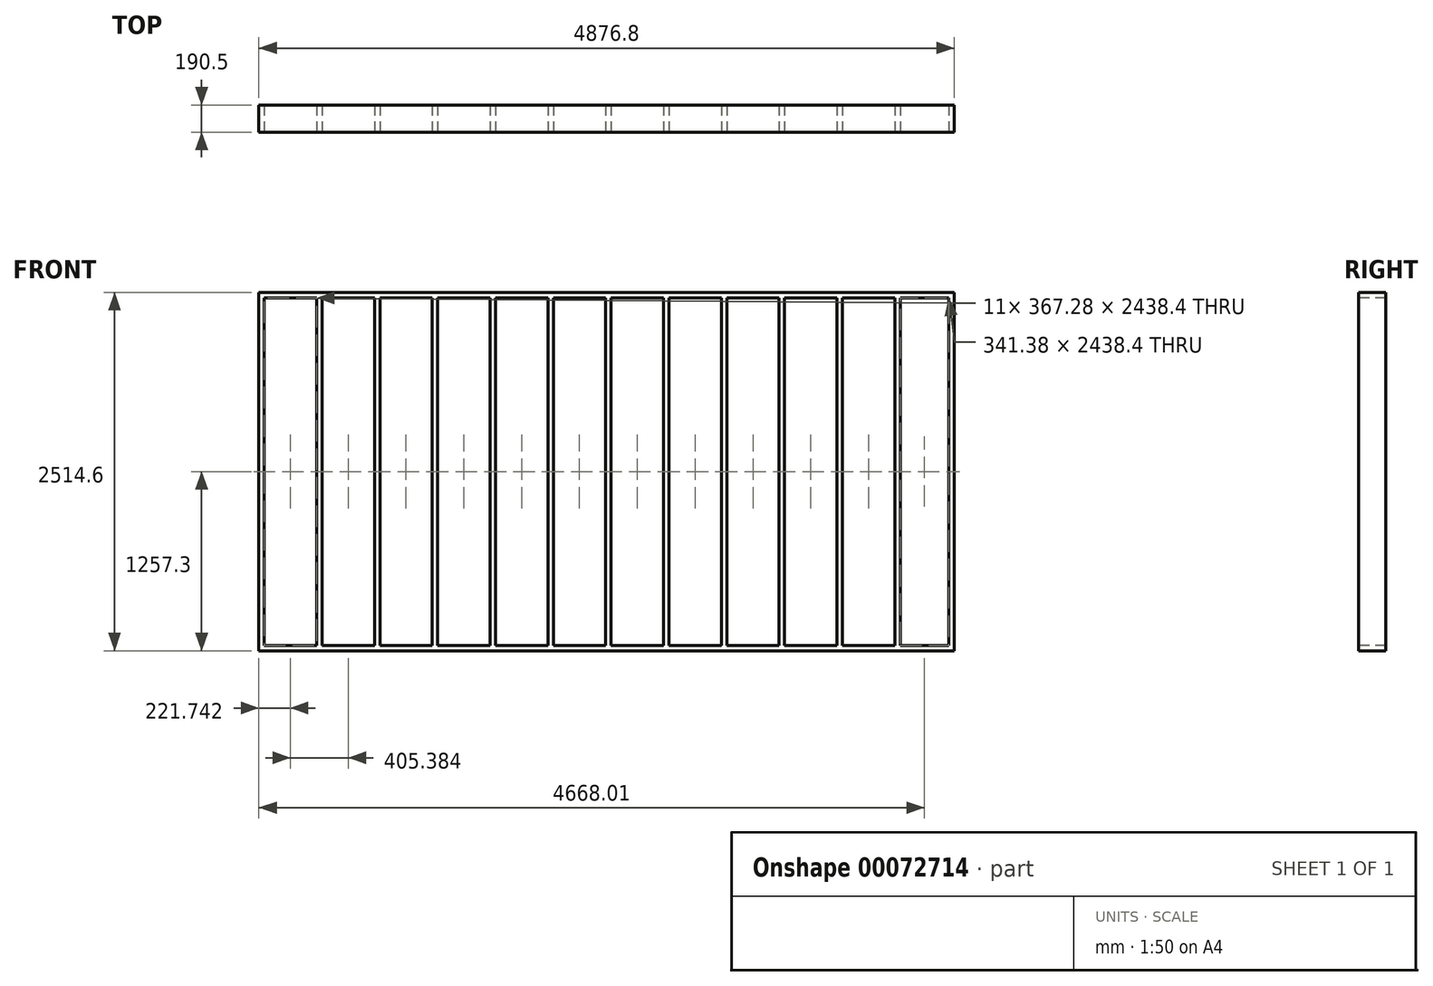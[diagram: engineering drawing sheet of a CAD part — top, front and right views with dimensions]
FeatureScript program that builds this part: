
annotation { "Feature Type Name" : "Feature", "Feature Type Description" : "" }
export const myFeature = defineFeature(function(context is Context, id is Id, definition is map)
    precondition{}
    {
        {
            var Q0;
            Q0=qCreatedBy(makeId("Top.planeOp"),FACE);
            var sketch = newSketch(context, id + "F0", { "sketchPlane" : qUnion([Q0])});
            skLineSegment(sketch, "E0.bottom", {"start": v(0, 0) * mm, "end": v(4876.8, 0) * mm});
            skLineSegment(sketch, "E0.top", {"start": v(0, 190.5) * mm, "end": v(4876.8, 190.5) * mm});
            skLineSegment(sketch, "E0.left", {"start": v(0, 0) * mm, "end": v(0, 190.5) * mm});
            skLineSegment(sketch, "E0.right", {"start": v(4876.8, 0) * mm, "end": v(4876.8, 190.5) * mm});
            skSolve(sketch);
        }
        {
            var Q0;
            Q0=makeQuery(id+"F0.imprint","IMPRINT",FACE,{"disambiguationData":[TD([[makeQuery(id+"F0.imprint","IMPRINT",EDGE,{"derivedFrom":sQuery(id+"F0.wireOp",EDGE,"E0.bottom")}),1.0]])]});
            extrude(context, id + "F1", {"entities" : qUnion([Q0]), "depth" : 38.1 * mm});
        }
        {
            var Q0;
            Q0=makeQuery(id+"F1.opExtrude","CAP_FACE",FACE,{"disambiguationData":[OSD([sQuery(id+"F0.wireOp",EDGE,"E0.bottom"),sQuery(id+"F0.wireOp",EDGE,"E0.top"),sQuery(id+"F0.wireOp",EDGE,"E0.left"),sQuery(id+"F0.wireOp",EDGE,"E0.right")])],"isStart":false});
            var sketch = newSketch(context, id + "F2", { "sketchPlane" : qUnion([Q0])});
            skLineSegment(sketch, "E1.bottom", {"start": v(0, 190.5) * mm, "end": v(38.1, 190.5) * mm});
            skLineSegment(sketch, "E1.top", {"start": v(0, 0) * mm, "end": v(38.1, 0) * mm});
            skLineSegment(sketch, "E1.left", {"start": v(0, 190.5) * mm, "end": v(0, 0) * mm});
            skLineSegment(sketch, "E1.right", {"start": v(38.1, 190.5) * mm, "end": v(38.1, 0) * mm});
            skLineSegment(sketch, "E2.1.0.0", {"start": v(405.38, 190.5) * mm, "end": v(443.48, 190.5) * mm});
            skLineSegment(sketch, "E2.1.0.1", {"start": v(405.38, 0) * mm, "end": v(443.48, 0) * mm});
            skLineSegment(sketch, "E2.1.0.2", {"start": v(405.38, 190.5) * mm, "end": v(405.38, 0) * mm});
            skLineSegment(sketch, "E2.1.0.3", {"start": v(443.48, 190.5) * mm, "end": v(443.48, 0) * mm});
            skLineSegment(sketch, "E2.2.0.0", {"start": v(810.77, 190.5) * mm, "end": v(848.87, 190.5) * mm});
            skLineSegment(sketch, "E2.2.0.1", {"start": v(810.77, 0) * mm, "end": v(848.87, 0) * mm});
            skLineSegment(sketch, "E2.2.0.2", {"start": v(810.77, 190.5) * mm, "end": v(810.77, 0) * mm});
            skLineSegment(sketch, "E2.2.0.3", {"start": v(848.87, 190.5) * mm, "end": v(848.87, 0) * mm});
            skLineSegment(sketch, "E2.3.0.0", {"start": v(1216.15, 190.5) * mm, "end": v(1254.25, 190.5) * mm});
            skLineSegment(sketch, "E2.3.0.1", {"start": v(1216.15, 0) * mm, "end": v(1254.25, 0) * mm});
            skLineSegment(sketch, "E2.3.0.2", {"start": v(1216.15, 190.5) * mm, "end": v(1216.15, 0) * mm});
            skLineSegment(sketch, "E2.3.0.3", {"start": v(1254.25, 190.5) * mm, "end": v(1254.25, 0) * mm});
            skLineSegment(sketch, "E2.4.0.0", {"start": v(1621.54, 190.5) * mm, "end": v(1659.64, 190.5) * mm});
            skLineSegment(sketch, "E2.4.0.1", {"start": v(1621.54, 0) * mm, "end": v(1659.64, 0) * mm});
            skLineSegment(sketch, "E2.4.0.2", {"start": v(1621.54, 190.5) * mm, "end": v(1621.54, 0) * mm});
            skLineSegment(sketch, "E2.4.0.3", {"start": v(1659.64, 190.5) * mm, "end": v(1659.64, 0) * mm});
            skLineSegment(sketch, "E2.5.0.0", {"start": v(2026.92, 190.5) * mm, "end": v(2065.02, 190.5) * mm});
            skLineSegment(sketch, "E2.5.0.1", {"start": v(2026.92, 0) * mm, "end": v(2065.02, 0) * mm});
            skLineSegment(sketch, "E2.5.0.2", {"start": v(2026.92, 190.5) * mm, "end": v(2026.92, 0) * mm});
            skLineSegment(sketch, "E2.5.0.3", {"start": v(2065.02, 190.5) * mm, "end": v(2065.02, 0) * mm});
            skLineSegment(sketch, "E2.6.0.0", {"start": v(2432.3, 190.5) * mm, "end": v(2470.4, 190.5) * mm});
            skLineSegment(sketch, "E2.6.0.1", {"start": v(2432.3, 0) * mm, "end": v(2470.4, 0) * mm});
            skLineSegment(sketch, "E2.6.0.2", {"start": v(2432.3, 190.5) * mm, "end": v(2432.3, 0) * mm});
            skLineSegment(sketch, "E2.6.0.3", {"start": v(2470.4, 190.5) * mm, "end": v(2470.4, 0) * mm});
            skLineSegment(sketch, "E2.7.0.0", {"start": v(2837.69, 190.5) * mm, "end": v(2875.79, 190.5) * mm});
            skLineSegment(sketch, "E2.7.0.1", {"start": v(2837.69, 0) * mm, "end": v(2875.79, 0) * mm});
            skLineSegment(sketch, "E2.7.0.2", {"start": v(2837.69, 190.5) * mm, "end": v(2837.69, 0) * mm});
            skLineSegment(sketch, "E2.7.0.3", {"start": v(2875.79, 190.5) * mm, "end": v(2875.79, 0) * mm});
            skLineSegment(sketch, "E2.8.0.0", {"start": v(3243.07, 190.5) * mm, "end": v(3281.17, 190.5) * mm});
            skLineSegment(sketch, "E2.8.0.1", {"start": v(3243.07, 0) * mm, "end": v(3281.17, 0) * mm});
            skLineSegment(sketch, "E2.8.0.2", {"start": v(3243.07, 190.5) * mm, "end": v(3243.07, 0) * mm});
            skLineSegment(sketch, "E2.8.0.3", {"start": v(3281.17, 190.5) * mm, "end": v(3281.17, 0) * mm});
            skLineSegment(sketch, "E2.9.0.0", {"start": v(3648.46, 190.5) * mm, "end": v(3686.56, 190.5) * mm});
            skLineSegment(sketch, "E2.9.0.1", {"start": v(3648.46, 0) * mm, "end": v(3686.56, 0) * mm});
            skLineSegment(sketch, "E2.9.0.2", {"start": v(3648.46, 190.5) * mm, "end": v(3648.46, 0) * mm});
            skLineSegment(sketch, "E2.9.0.3", {"start": v(3686.56, 190.5) * mm, "end": v(3686.56, 0) * mm});
            skLineSegment(sketch, "E2.10.0.0", {"start": v(4053.84, 190.5) * mm, "end": v(4091.94, 190.5) * mm});
            skLineSegment(sketch, "E2.10.0.1", {"start": v(4053.84, 0) * mm, "end": v(4091.94, 0) * mm});
            skLineSegment(sketch, "E2.10.0.2", {"start": v(4053.84, 190.5) * mm, "end": v(4053.84, 0) * mm});
            skLineSegment(sketch, "E2.10.0.3", {"start": v(4091.94, 190.5) * mm, "end": v(4091.94, 0) * mm});
            skLineSegment(sketch, "E2.11.0.0", {"start": v(4459.22, 190.5) * mm, "end": v(4497.32, 190.5) * mm});
            skLineSegment(sketch, "E2.11.0.1", {"start": v(4459.22, 0) * mm, "end": v(4497.32, 0) * mm});
            skLineSegment(sketch, "E2.11.0.2", {"start": v(4459.22, 190.5) * mm, "end": v(4459.22, 0) * mm});
            skLineSegment(sketch, "E2.11.0.3", {"start": v(4497.32, 190.5) * mm, "end": v(4497.32, 0) * mm});
            skLineSegment(sketch, "E2.direction1", {"start": v(0, 190.5) * mm, "end": v(405.38, 190.5) * mm, "construction": true});
            skLineSegment(sketch, "E3.bottom", {"start": v(4876.8, 190.5) * mm, "end": v(4838.7, 190.5) * mm});
            skLineSegment(sketch, "E3.top", {"start": v(4876.8, 0) * mm, "end": v(4838.7, 0) * mm});
            skLineSegment(sketch, "E3.left", {"start": v(4876.8, 190.5) * mm, "end": v(4876.8, 0) * mm});
            skLineSegment(sketch, "E3.right", {"start": v(4838.7, 190.5) * mm, "end": v(4838.7, 0) * mm});
            skSolve(sketch);
        }
        {
            var Q0;
            Q0 = qSketchRegion(id + "F2", true);
            extrude(context, id + "F3", {"entities" : qUnion([Q0]), "operationType" : NewBodyOperationType.ADD, "depth" : 2438.4 * mm});
        }
        {
            var Q0;
            Q0=makeQuery(id+"F3.opExtrude","CAP_FACE",FACE,{"disambiguationData":[OSD([sQuery(id+"F2.wireOp",EDGE,"E1.bottom"),sQuery(id+"F2.wireOp",EDGE,"E1.top"),sQuery(id+"F2.wireOp",EDGE,"E1.left"),sQuery(id+"F2.wireOp",EDGE,"E1.right")])],"isStart":false});
            var sketch = newSketch(context, id + "F4", { "sketchPlane" : qUnion([Q0])});
            skLineSegment(sketch, "E4.bottom", {"start": v(0, 190.5) * mm, "end": v(4876.8, 190.5) * mm});
            skLineSegment(sketch, "E4.top", {"start": v(0, 0) * mm, "end": v(4876.8, 0) * mm});
            skLineSegment(sketch, "E4.left", {"start": v(0, 190.5) * mm, "end": v(0, 0) * mm});
            skLineSegment(sketch, "E4.right", {"start": v(4876.8, 190.5) * mm, "end": v(4876.8, 0) * mm});
            skSolve(sketch);
        }
        {
            var Q0;
            Q0 = qSketchRegion(id + "F4", true);
            extrude(context, id + "F5", {"entities" : qUnion([Q0]), "operationType" : NewBodyOperationType.ADD, "depth" : 38.1 * mm});
        }
    });
